# Revit family: Hager-Orion-IP65-D160-Cl.I-Steel_encl-630A-NoHosted-ES-es
name_source: partatom
category: Electrical Equipment
units: mm (PartAtom-declared; Revit-internal decimal feet)

## family parameters
Always vertical = Yes
Cut with Voids When Loaded = No
Panel Configuration = Two Columns, Circuits Across
Part Type = Panelboard
Room Calculation Point = No
Round Connector Dimension = Use Diameter
Shared = No
Work Plane-Based = Yes

## types (3) — shared parameters
Default Elevation = 1219 mm
EF000003 - Tipo de montaje = EV000384 - Montado superficial (escayola)
EF000007 - Color = EV000270 - Gris
EF000049 - Profundidad = 160 mm  [stored 0.524934 ft]
EF000116 - Número RAL = 7035
EF000118 - Con placa de montaje = Yes
EF000339 - Tipo de cubierta = EV004216 - Puerta
EF001088 - Posibilidad de extensión = No
EF001131 - Profundidad interna = 160 mm  [stored 0.524934 ft]
EF001596 - Material de la carcasa = EV000179 - Acero
EF003532 - Adecuado para uso en exteriores = No
EF004293 - Resistencia al impacto (IK) = EV008784 - IK10
EF004464 - Tipo de puerta = EV002646 - Único
EF005474 - Grado de protección (IP) = EV006421 - IP65
EF006244 - Tapa/puerta transparente = No
EF006306 - Con cierre = Yes
EF007800 - Adecuado para la protección contra rayos = No
EF008873 - Corriente nominal (In) = 630 A
EF009170 - Espesor del material de la caja = 2 mm  [stored 0.00656168 ft]
EF009171 - Espesor puerta/tapa = 2 mm  [stored 0.00656168 ft]
EF009212 - Versión de la cubierta = EV009916 - Con muesca
EF015940 - Tapa con alivio de sobrepresión = No
HG000002 - Con puerta o tapa = Yes
HG000003 - Gama = Orion
HG000006 - Empotrado = No
HG000009 - Puerta batiente doble = No
HG000010 - Puertas asimétricas = No
HG000023 - Caja de doble sección = No
HG000024 - Altura de la sección inferior = 600 mm
HG000026 - Instalación en suelo = No
Manufacturer = Hager
Type Comments = Orion
zero-valued in all types: EF000218 - Profundidad de instalación, EF002950 - Anchura de unidades de división, EF004427 - Número de módulos, HG000027 - Altura de zócalo

## per-type parameters (varying)
| type | EF000008 - Anchura | EF000040 - Altura | EF000266 - Número de filas | EF000437 - Número de entradas de conductos de cables | EF009554 - Número de aberturas para placas-brida | HG000004 - Referencia del fabricante |
| Montado superficial (escayola) IP65 A200 A250 P160  - FL701L | 200 mm  [stored 0.656168 ft] | 250 mm  [stored 0.82021 ft] | 0 | 2 | 2 | FL701L |
| Montado superficial (escayola) IP65 A250 A300 P160  - FL702L | 250 mm  [stored 0.82021 ft] | 300 mm | 1 | 1 | 1 | FL702L |
| Montado superficial (escayola) IP65 A300 A300 P160  - FL703L | 300 mm | 300 mm | 0 | 2 | 2 | FL703L |

note: [stored X ft] marks values corroborated as IEEE doubles in the binary element streams (Revit-internal decimal feet)

## geometry (parser evidence)
native form markers: Blend x4, Sweep x10
no freeform markers — native parametric forms only
